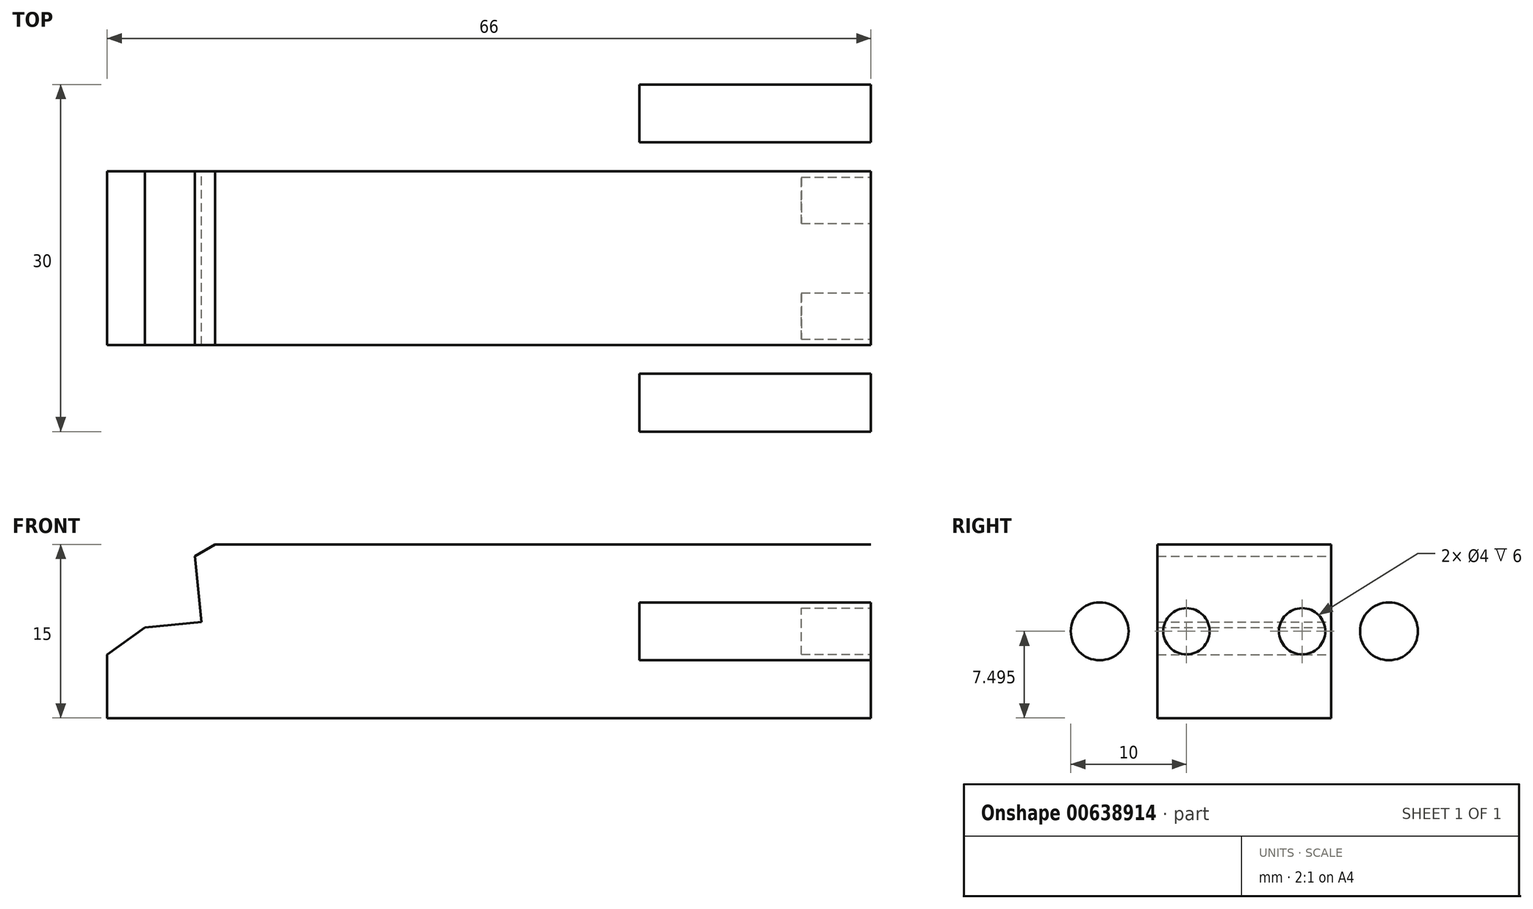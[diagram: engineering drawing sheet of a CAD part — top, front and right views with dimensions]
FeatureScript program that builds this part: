
annotation { "Feature Type Name" : "Feature", "Feature Type Description" : "" }
export const myFeature = defineFeature(function(context is Context, id is Id, definition is map)
    precondition{}
    {
        {
            var Q0;
            Q0=qCreatedBy(makeId("Front.planeOp"),FACE);
            var sketch = newSketch(context, id + "F0", { "sketchPlane" : qUnion([Q0])});
            skLineSegment(sketch, "E0", {"start": v(61.53, -23.2) * mm, "end": v(61.53, -38.2) * mm});
            skLineSegment(sketch, "E1", {"start": v(15.53, -38.2) * mm, "end": v(81.53, -38.2) * mm});
            skLineSegment(sketch, "E2", {"start": v(81.53, -23.2) * mm, "end": v(81.53, -38.2) * mm});
            skLineSegment(sketch, "E3", {"start": v(24.85, -23.2) * mm, "end": v(81.53, -23.2) * mm});
            skLineSegment(sketch, "E4", {"start": v(15.53, -38.2) * mm, "end": v(15.53, -32.71) * mm});
            skLineSegment(sketch, "E5", {"start": v(23.12, -24.2) * mm, "end": v(24.85, -23.2) * mm});
            skLineSegment(sketch, "E6", {"start": v(23.68, -29.9) * mm, "end": v(18.78, -30.38) * mm});
            skLineSegment(sketch, "E7", {"start": v(15.53, -32.71) * mm, "end": v(18.78, -30.38) * mm});
            skLineSegment(sketch, "E8", {"start": v(23.12, -24.2) * mm, "end": v(23.68, -29.9) * mm});
            skLineSegment(sketch, "E9", {"start": v(59.53, -30.7) * mm, "end": v(83.53, -30.7) * mm});
            skLineSegment(sketch, "E10", {"start": v(-58.53, -38.2) * mm, "end": v(-58.53, -23.2) * mm});
            skLineSegment(sketch, "E11", {"start": v(-73.53, -23.2) * mm, "end": v(-73.53, -38.2) * mm});
            skCircle(sketch, "E12", {"center": v(-61.03, -30.7) * mm, "radius": 2 * mm});
            skCircle(sketch, "E13", {"center": v(-71.03, -30.7) * mm, "radius": 2 * mm});
            skCircle(sketch, "E14", {"center": v(-53.53, -30.7) * mm, "radius": 2.5 * mm});
            skCircle(sketch, "E15", {"center": v(-78.53, -30.7) * mm, "radius": 2.5 * mm});
            skLineSegment(sketch, "E16", {"start": v(-48.53, -38.2) * mm, "end": v(-83.53, -38.2) * mm});
            skLineSegment(sketch, "E17", {"start": v(-73.53, -32.71) * mm, "end": v(-58.53, -32.71) * mm});
            skLineSegment(sketch, "E18", {"start": v(-73.53, -30.38) * mm, "end": v(-58.53, -30.38) * mm});
            skLineSegment(sketch, "E19", {"start": v(-73.53, -29.9) * mm, "end": v(-58.53, -29.9) * mm});
            skLineSegment(sketch, "E20", {"start": v(-73.53, -24.2) * mm, "end": v(-58.53, -24.2) * mm});
            skLineSegment(sketch, "E21", {"start": v(-48.53, -23.2) * mm, "end": v(-48.53, -38.2) * mm});
            skLineSegment(sketch, "E22", {"start": v(-48.53, -23.2) * mm, "end": v(-83.53, -23.2) * mm});
            skLineSegment(sketch, "E23", {"start": v(-83.53, -23.2) * mm, "end": v(-83.53, -38.2) * mm});
            skLineSegment(sketch, "E24", {"start": v(61.53, 3.2) * mm, "end": v(81.53, 3.2) * mm});
            skLineSegment(sketch, "E25", {"start": v(61.53, 13.2) * mm, "end": v(15.53, 13.2) * mm});
            skLineSegment(sketch, "E26", {"start": v(61.53, 28.2) * mm, "end": v(15.53, 28.2) * mm});
            skLineSegment(sketch, "E27", {"start": v(61.53, 38.2) * mm, "end": v(81.53, 38.2) * mm});
            skLineSegment(sketch, "E28", {"start": v(81.53, 3.2) * mm, "end": v(81.53, 38.2) * mm});
            skLineSegment(sketch, "E29", {"start": v(61.53, 3.2) * mm, "end": v(61.53, 13.2) * mm});
            skLineSegment(sketch, "E30", {"start": v(15.53, 13.2) * mm, "end": v(15.53, 28.2) * mm});
            skLineSegment(sketch, "E31", {"start": v(61.53, 28.2) * mm, "end": v(61.53, 38.2) * mm});
            skLineSegment(sketch, "E32", {"start": v(23.12, 13.2) * mm, "end": v(23.12, 28.2) * mm});
            skLineSegment(sketch, "E33", {"start": v(23.68, 13.2) * mm, "end": v(23.68, 28.2) * mm});
            skLineSegment(sketch, "E34", {"start": v(24.85, 13.2) * mm, "end": v(24.85, 28.2) * mm});
            skLineSegment(sketch, "E35", {"start": v(18.78, 13.2) * mm, "end": v(18.78, 28.2) * mm});
            skSolve(sketch);
        }
        {
            var Q0;
            {var subQ3=sQuery(id+"F0.wireOp",EDGE,"E4");Q0=makeQuery(id+"F0.imprint","IMPRINT",FACE,{"disambiguationData":[TD([[makeQuery(id+"F0.imprint","IMPRINT",EDGE,{"derivedFrom":subQ3}),-1.0]])]});}
            var Q1;
            {var subQ0=sQuery(id+"F0.wireOp",EDGE,"E3");var subQ1=sQuery(id+"F0.wireOp",EDGE,"E0");var subQ2=makeQuery(id+"F0.imprint","INTERSECT",VERTEX,{"derivedFrom":[subQ1,subQ0]});Q1=makeQuery(id+"F0.imprint","IMPRINT",FACE,{"disambiguationData":[TD([[makeQuery(id+"F0.imprint","IMPRINT",EDGE,{"disambiguationData":[TD([[subQ2,-1.0]])],"derivedFrom":subQ1}),1.0]])]});}
            var Q2;
            {var subQ0=sQuery(id+"F0.wireOp",EDGE,"E1");var subQ1=sQuery(id+"F0.wireOp",EDGE,"E0");var subQ2=makeQuery(id+"F0.imprint","INTERSECT",VERTEX,{"derivedFrom":[subQ1,subQ0]});Q2=makeQuery(id+"F0.imprint","IMPRINT",FACE,{"disambiguationData":[TD([[makeQuery(id+"F0.imprint","IMPRINT",EDGE,{"disambiguationData":[TD([[subQ2,1.0]])],"derivedFrom":subQ1}),1.0]])]});}
            extrude(context, id + "F1", {"entities" : qUnion([Q0, Q1, Q2]), "depth" : 35 * mm, "offsetDistance" : 25 * mm});
        }
        {
            var Q0;
            Q0=makeQuery(id+"F1.opExtrude","SWEPT_FACE",FACE,{"disambiguationData":[OSD([sQuery(id+"F0.wireOp",EDGE,"E3")])]});
            var sketch = newSketch(context, id + "F2", { "sketchPlane" : qUnion([Q0])});
            skLineSegment(sketch, "E36.0", {"start": v(24.85, 0) * mm, "end": v(81.53, 0) * mm});
            skLineSegment(sketch, "E37.0", {"start": v(81.53, -35) * mm, "end": v(81.53, 0) * mm});
            skLineSegment(sketch, "E38.0", {"start": v(24.85, -35) * mm, "end": v(81.53, -35) * mm});
            skLineSegment(sketch, "E39.0", {"start": v(24.85, -35) * mm, "end": v(24.85, 0) * mm});
            skLineSegment(sketch, "E40", {"start": v(61.53, -35) * mm, "end": v(81.53, -35) * mm});
            skLineSegment(sketch, "E41", {"start": v(61.53, -25) * mm, "end": v(15.53, -25) * mm});
            skLineSegment(sketch, "E42", {"start": v(61.53, -10) * mm, "end": v(15.53, -10) * mm});
            skLineSegment(sketch, "E43", {"start": v(61.53, 0) * mm, "end": v(81.53, 0) * mm});
            skLineSegment(sketch, "E44", {"start": v(61.53, -35) * mm, "end": v(61.53, -25) * mm});
            skLineSegment(sketch, "E45", {"start": v(15.53, -25) * mm, "end": v(15.53, -10) * mm});
            skLineSegment(sketch, "E46", {"start": v(61.53, -10) * mm, "end": v(61.53, 0) * mm});
            skLineSegment(sketch, "E47", {"start": v(23.12, -25) * mm, "end": v(23.12, -10) * mm});
            skLineSegment(sketch, "E48", {"start": v(23.68, -25) * mm, "end": v(23.68, -10) * mm});
            skLineSegment(sketch, "E49", {"start": v(24.85, -25) * mm, "end": v(24.85, -10) * mm});
            skLineSegment(sketch, "E50", {"start": v(18.78, -25) * mm, "end": v(18.78, -10) * mm});
            skLineSegment(sketch, "E51.0", {"start": v(15.53, 0) * mm, "end": v(18.78, 0) * mm});
            skLineSegment(sketch, "E52.0", {"start": v(23.68, 0) * mm, "end": v(18.78, 0) * mm});
            skLineSegment(sketch, "E53.0", {"start": v(23.12, 0) * mm, "end": v(24.85, 0) * mm});
            skLineSegment(sketch, "E54.0", {"start": v(23.68, -35) * mm, "end": v(18.78, -35) * mm});
            skLineSegment(sketch, "E55.0", {"start": v(15.53, -35) * mm, "end": v(18.78, -35) * mm});
            skLineSegment(sketch, "E56.0", {"start": v(15.53, -35) * mm, "end": v(15.53, 0) * mm});
            skLineSegment(sketch, "E57.0", {"start": v(23.12, -35) * mm, "end": v(24.85, -35) * mm});
            skSolve(sketch);
        }
        {
            var Q0;
            {var subQ0=sQuery(id+"F2.wireOp",EDGE,"E36.0");Q0=makeQuery(id+"F2.imprint","IMPRINT",FACE,{"disambiguationData":[TD([[makeQuery(id+"F2.imprint","IMPRINT",EDGE,{"derivedFrom":subQ0}),-1.0]])]});}
            var Q1;
            {var subQ3=sQuery(id+"F2.wireOp",EDGE,"E51.0");Q1=makeQuery(id+"F2.imprint","IMPRINT",FACE,{"disambiguationData":[TD([[makeQuery(id+"F2.imprint","IMPRINT",EDGE,{"derivedFrom":subQ3}),-1.0]])]});}
            var Q2;
            {var subQ0=sQuery(id+"F2.wireOp",EDGE,"E38.0");Q2=makeQuery(id+"F2.imprint","IMPRINT",FACE,{"disambiguationData":[TD([[makeQuery(id+"F2.imprint","IMPRINT",EDGE,{"derivedFrom":subQ0}),1.0]])]});}
            var Q3;
            {var subQ11=sQuery(id+"F2.wireOp",EDGE,"E54.0");Q3=makeQuery(id+"F2.imprint","IMPRINT",FACE,{"disambiguationData":[TD([[makeQuery(id+"F2.imprint","IMPRINT",EDGE,{"derivedFrom":subQ11}),-1.0]])]});}
            extrude(context, id + "F3", {"entities" : qUnion([Q0, Q1, Q2, Q3]), "operationType" : NewBodyOperationType.REMOVE, "endBound" : BoundingType.THROUGH_ALL, "oppositeDirection" : true, "depth" : 25 * mm, "offsetDistance" : 25 * mm});
        }
        {
            var Q0;
            Q0=makeQuery(id+"F3.boolean.opBoolean","COPY",FACE,{"derivedFrom":makeQuery(id+"F3.opExtrude","SWEPT_FACE",FACE,{"disambiguationData":[OSD([sQuery(id+"F2.wireOp",EDGE,"E44")])]})});
            var sketch = newSketch(context, id + "F4", { "sketchPlane" : qUnion([Q0])});
            skLineSegment(sketch, "E58.0", {"start": v(35, -38.2) * mm, "end": v(25, -38.2) * mm});
            skLineSegment(sketch, "E59.0", {"start": v(35, -38.2) * mm, "end": v(35, -23.2) * mm});
            skLineSegment(sketch, "E60.0", {"start": v(35, -23.2) * mm, "end": v(25, -23.2) * mm});
            skLineSegment(sketch, "E61", {"start": v(25, -38.2) * mm, "end": v(25, -23.2) * mm});
            skLineSegment(sketch, "E62", {"start": v(10, -23.2) * mm, "end": v(10, -38.2) * mm});
            skCircle(sketch, "E63", {"center": v(22.5, -30.7) * mm, "radius": 2 * mm});
            skCircle(sketch, "E64", {"center": v(12.5, -30.7) * mm, "radius": 2 * mm});
            skCircle(sketch, "E65", {"center": v(30, -30.7) * mm, "radius": 2.5 * mm});
            skCircle(sketch, "E66", {"center": v(5, -30.7) * mm, "radius": 2.5 * mm});
            skLineSegment(sketch, "E67", {"start": v(35, -38.2) * mm, "end": v(0, -38.2) * mm});
            skLineSegment(sketch, "E68", {"start": v(10, -32.71) * mm, "end": v(25, -32.71) * mm});
            skLineSegment(sketch, "E69", {"start": v(10, -30.38) * mm, "end": v(25, -30.38) * mm});
            skLineSegment(sketch, "E70", {"start": v(10, -29.9) * mm, "end": v(25, -29.9) * mm});
            skLineSegment(sketch, "E71", {"start": v(10, -24.2) * mm, "end": v(25, -24.2) * mm});
            skLineSegment(sketch, "E72", {"start": v(35, -23.2) * mm, "end": v(35, -38.2) * mm});
            skLineSegment(sketch, "E73", {"start": v(35, -23.2) * mm, "end": v(0, -23.2) * mm});
            skLineSegment(sketch, "E74", {"start": v(0, -23.2) * mm, "end": v(0, -38.2) * mm});
            skSolve(sketch);
        }
        {
            var Q0;
            Q0=makeQuery(id+"F4.imprint","IMPRINT",FACE,{"disambiguationData":[TD([[makeQuery(id+"F4.imprint","IMPRINT",EDGE,{"derivedFrom":sQuery(id+"F4.wireOp",EDGE,"E65")}),-1.0]])]});
            var Q1;
            Q1=makeQuery(id+"F4.imprint","IMPRINT",FACE,{"disambiguationData":[TD([[makeQuery(id+"F4.imprint","IMPRINT",EDGE,{"derivedFrom":sQuery(id+"F4.wireOp",EDGE,"E66")}),-1.0]])]});
            extrude(context, id + "F5", {"entities" : qUnion([Q0, Q1]), "operationType" : NewBodyOperationType.REMOVE, "endBound" : BoundingType.THROUGH_ALL, "oppositeDirection" : true, "depth" : 25 * mm, "offsetDistance" : 25 * mm});
        }
        {
            var Q0;
            Q0=makeQuery(id+"F1.opExtrude","SWEPT_FACE",FACE,{"disambiguationData":[OSD([sQuery(id+"F0.wireOp",EDGE,"E2")])]});
            var sketch = newSketch(context, id + "F6", { "sketchPlane" : qUnion([Q0])});
            skCircle(sketch, "E75.0", {"center": v(-22.5, -30.7) * mm, "radius": 2 * mm});
            skCircle(sketch, "E76.0", {"center": v(-12.5, -30.7) * mm, "radius": 2 * mm});
            skSolve(sketch);
        }
        {
            var Q0;
            Q0=qCreatedBy(makeId("Right.planeOp"),FACE);
            var sketch = newSketch(context, id + "F7", { "sketchPlane" : qUnion([Q0])});
            skLineSegment(sketch, "E77.bottom", {"start": v(-42.24, 59.53) * mm, "end": v(-65.77, 59.53) * mm});
            skLineSegment(sketch, "E77.top", {"start": v(-42.24, 47.4) * mm, "end": v(-65.77, 47.4) * mm});
            skLineSegment(sketch, "E77.left", {"start": v(-42.24, 59.53) * mm, "end": v(-42.24, 47.4) * mm});
            skLineSegment(sketch, "E77.right", {"start": v(-65.77, 59.53) * mm, "end": v(-65.77, 47.4) * mm});
            skSolve(sketch);
        }
        {
            var Q0;
            Q0 = qSketchRegion(id + "F7", true);
            extrude(context, id + "F8", {"entities" : qUnion([Q0]), "depth" : 25 * mm, "offsetDistance" : 25 * mm});
        }
        {
            var Q0;
            Q0=makeQuery(id+"F8.opExtrude","SWEPT_BODY",BODY,{"disambiguationData":[OSD([sQuery(id+"F7.wireOp",EDGE,"E77.bottom"),sQuery(id+"F7.wireOp",EDGE,"E77.top"),sQuery(id+"F7.wireOp",EDGE,"E77.left"),sQuery(id+"F7.wireOp",EDGE,"E77.right")])]});
            transform(context, id + "F9", {"entities" : qUnion([Q0]), "transformType" : TransformType.TRANSLATION_3D, "dx" : 0 * mm, "dy" : -65 * mm, "dz" : 0 * mm, "makeCopy" : true});
        }
        {
            var Q0;
            Q0=makeQuery(id+"F9.opPattern","COPY",BODY,{"derivedFrom":makeQuery(id+"F8.opExtrude","SWEPT_BODY",BODY,{"disambiguationData":[OSD([sQuery(id+"F7.wireOp",EDGE,"E77.bottom"),sQuery(id+"F7.wireOp",EDGE,"E77.top"),sQuery(id+"F7.wireOp",EDGE,"E77.left"),sQuery(id+"F7.wireOp",EDGE,"E77.right")])]}),"instanceName":"1"});
            deleteBodies(context, id + "F10", {"entities" : qUnion([Q0])});
        }
        {
            var Q0;
            Q0=makeQuery(id+"F6.imprint","IMPRINT",FACE,{"disambiguationData":[TD([[makeQuery(id+"F6.imprint","IMPRINT",EDGE,{"derivedFrom":sQuery(id+"F6.wireOp",EDGE,"E76.0")}),1.0]])]});
            var Q1;
            Q1=makeQuery(id+"F6.imprint","IMPRINT",FACE,{"disambiguationData":[TD([[makeQuery(id+"F6.imprint","IMPRINT",EDGE,{"derivedFrom":sQuery(id+"F6.wireOp",EDGE,"E75.0")}),1.0]])]});
            extrude(context, id + "F11", {"entities" : qUnion([Q0, Q1]), "operationType" : NewBodyOperationType.REMOVE, "oppositeDirection" : true, "depth" : 6 * mm, "offsetDistance" : 25 * mm});
        }
        {
            var Q0;
            Q0=makeQuery(id+"F8.opExtrude","SWEPT_BODY",BODY,{"disambiguationData":[OSD([sQuery(id+"F7.wireOp",EDGE,"E77.bottom"),sQuery(id+"F7.wireOp",EDGE,"E77.top"),sQuery(id+"F7.wireOp",EDGE,"E77.left"),sQuery(id+"F7.wireOp",EDGE,"E77.right")])]});
            deleteBodies(context, id + "F12", {"entities" : qUnion([Q0])});
        }
    });
